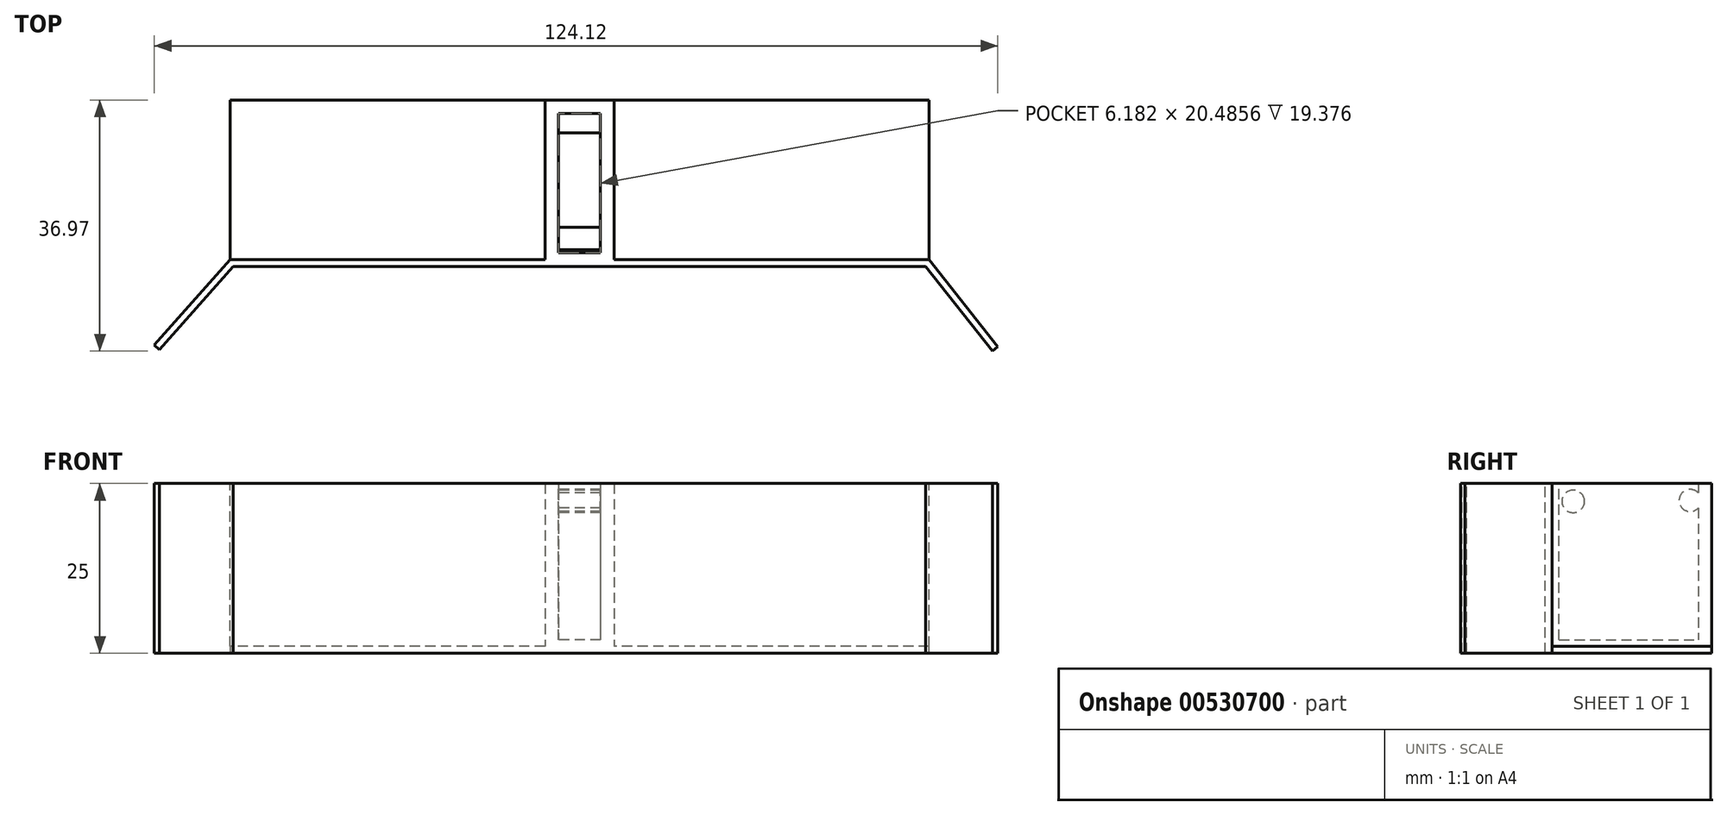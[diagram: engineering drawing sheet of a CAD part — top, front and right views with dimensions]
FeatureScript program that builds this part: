
annotation { "Feature Type Name" : "Feature", "Feature Type Description" : "" }
export const myFeature = defineFeature(function(context is Context, id is Id, definition is map)
    precondition{}
    {
        {
            var Q0;
            Q0=qCreatedBy(makeId("Top.planeOp"),FACE);
            var sketch = newSketch(context, id + "F0", { "sketchPlane" : qUnion([Q0])});
            skLineSegment(sketch, "E0.bottom", {"start": v(51.45, 11.74) * mm, "end": v(-51.45, 11.74) * mm});
            skLineSegment(sketch, "E0.top", {"start": v(51.45, -11.74) * mm, "end": v(-51.45, -11.74) * mm});
            skLineSegment(sketch, "E0.left", {"start": v(51.45, 11.74) * mm, "end": v(51.45, -11.74) * mm});
            skLineSegment(sketch, "E0.right", {"start": v(-51.45, 11.74) * mm, "end": v(-51.45, -11.74) * mm});
            skPoint(sketch, "E0.middle", {"position": v(0, 0) * mm});
            skLineSegment(sketch, "E1", {"start": v(-51.45, -11.74) * mm, "end": v(-62.57, -24.35) * mm});
            skLineSegment(sketch, "E2", {"start": v(51.45, -11.74) * mm, "end": v(61.55, -24.61) * mm});
            skSolve(sketch);
        }
        {
            var Q0;
            Q0=sQuery(id+"F0.wireOp",EDGE,"E2");
            extrude(context, id + "F1", {"bodyType" : ToolBodyType.SURFACE, "surfaceEntities" : qUnion([Q0]), "depth" : 25 * mm, "offsetDistance" : 25 * mm});
        }
        {
            var Q0;
            Q0=sQuery(id+"F0.wireOp",EDGE,"E1");
            extrude(context, id + "F2", {"bodyType" : ToolBodyType.SURFACE, "surfaceEntities" : qUnion([Q0]), "depth" : 25 * mm, "offsetDistance" : 25 * mm});
        }
        {
            var Q0;
            Q0=sQuery(id+"F0.wireOp",EDGE,"E0.top");
            extrude(context, id + "F3", {"bodyType" : ToolBodyType.SURFACE, "surfaceEntities" : qUnion([Q0]), "depth" : 25 * mm, "offsetDistance" : 25 * mm});
        }
        {
            var Q0;
            Q0=makeQuery(id+"F0.imprint","IMPRINT",FACE,{"disambiguationData":[TD([[makeQuery(id+"F0.imprint","IMPRINT",EDGE,{"derivedFrom":sQuery(id+"F0.wireOp",EDGE,"E0.bottom")}),1.0]])]});
            extrude(context, id + "F4", {"entities" : qUnion([Q0]), "depth" : 1 * mm, "offsetDistance" : 25 * mm});
        }
        {
            var Q0;
            Q0=makeQuery(id+"F3.opExtrude","SWEPT_FACE",FACE,{"disambiguationData":[OSD([sQuery(id+"F0.wireOp",EDGE,"E0.top")])]});
            extrude(context, id + "F5", {"entities" : qUnion([Q0]), "operationType" : NewBodyOperationType.ADD, "oppositeDirection" : true, "depth" : 1 * mm, "offsetDistance" : 25 * mm});
        }
        {
            var Q0;
            Q0=makeQuery(id+"F2.opExtrude","SWEPT_FACE",FACE,{"disambiguationData":[OSD([sQuery(id+"F0.wireOp",EDGE,"E1")])]});
            extrude(context, id + "F6", {"entities" : qUnion([Q0]), "operationType" : NewBodyOperationType.ADD, "oppositeDirection" : true, "depth" : 1 * mm, "offsetDistance" : 25 * mm});
        }
        {
            var Q0;
            Q0=makeQuery(id+"F1.opExtrude","SWEPT_FACE",FACE,{"disambiguationData":[OSD([sQuery(id+"F0.wireOp",EDGE,"E2")])]});
            extrude(context, id + "F7", {"entities" : qUnion([Q0]), "operationType" : NewBodyOperationType.ADD, "depth" : 1 * mm, "offsetDistance" : 25 * mm});
        }
        {
            var Q0;
            Q0=makeQuery(id+"F4.opExtrude","CAP_FACE",FACE,{"disambiguationData":[OSD([sQuery(id+"F0.wireOp",EDGE,"E0.bottom"),sQuery(id+"F0.wireOp",EDGE,"E0.top"),sQuery(id+"F0.wireOp",EDGE,"E0.left"),sQuery(id+"F0.wireOp",EDGE,"E0.right")])],"isStart":false});
            var sketch = newSketch(context, id + "F8", { "sketchPlane" : qUnion([Q0])});
            skLineSegment(sketch, "E3.bottom", {"start": v(5.1, -11.74) * mm, "end": v(-5.1, -11.74) * mm});
            skLineSegment(sketch, "E3.top", {"start": v(5.1, 11.74) * mm, "end": v(-5.1, 11.74) * mm});
            skLineSegment(sketch, "E3.left", {"start": v(5.1, -11.74) * mm, "end": v(5.1, 11.74) * mm});
            skLineSegment(sketch, "E3.right", {"start": v(-5.1, -11.74) * mm, "end": v(-5.1, 11.74) * mm});
            skPoint(sketch, "E3.middle", {"position": v(0, 0) * mm});
            skSolve(sketch);
        }
        {
            var Q0;
            Q0=makeQuery(id+"F8.imprint","IMPRINT",FACE,{"disambiguationData":[TD([[makeQuery(id+"F8.imprint","IMPRINT",EDGE,{"derivedFrom":sQuery(id+"F8.wireOp",EDGE,"E3.bottom")}),-1.0]])]});
            extrude(context, id + "F9", {"entities" : qUnion([Q0]), "operationType" : NewBodyOperationType.ADD, "depth" : 24 * mm, "offsetDistance" : 25 * mm});
        }
        {
            var Q0;
            {var subQ0=sQuery(id+"F0.wireOp",EDGE,"E2");var subQ1=sQuery(id+"F0.wireOp",EDGE,"E1");var subQ2=sQuery(id+"F0.wireOp",EDGE,"E0.top");Q0=makeQuery(id+"F9.boolean.opBoolean","MERGE",FACE,{"derivedFrom":[makeQuery(id+"F7.boolean.opBoolean","MERGE",FACE,{"derivedFrom":[makeQuery(id+"F6.boolean.opBoolean","MERGE",FACE,{"derivedFrom":[makeQuery(id+"F5.opExtrude","SWEPT_FACE",FACE,{"disambiguationData":[OSD([subQ2]),TDD([makeQuery(id+"F3.opExtrude","CAP_EDGE",EDGE,{"disambiguationData":[OSD([subQ2])],"isStart":false})])]}),makeQuery(id+"F6.opExtrude","SWEPT_FACE",FACE,{"disambiguationData":[OSD([subQ1]),TDD([makeQuery(id+"F2.opExtrude","CAP_EDGE",EDGE,{"disambiguationData":[OSD([subQ1])],"isStart":false})])]})]}),makeQuery(id+"F7.opExtrude","SWEPT_FACE",FACE,{"disambiguationData":[OSD([subQ0]),TDD([makeQuery(id+"F1.opExtrude","CAP_EDGE",EDGE,{"disambiguationData":[OSD([subQ0])],"isStart":false})])]})]}),makeQuery(id+"F9.opExtrude","CAP_FACE",FACE,{"disambiguationData":[OSD([sQuery(id+"F8.wireOp",EDGE,"E3.bottom"),sQuery(id+"F8.wireOp",EDGE,"E3.top"),sQuery(id+"F8.wireOp",EDGE,"E3.left"),sQuery(id+"F8.wireOp",EDGE,"E3.right")])],"isStart":false})]});}
            shell(context, id + "F10", {"entities" : qUnion([Q0]), "thickness" : 2 * mm});
        }
        {
            var Q0;
            Q0=makeQuery(id+"F9.opExtrude","SWEPT_FACE",FACE,{"disambiguationData":[OSD([sQuery(id+"F8.wireOp",EDGE,"E3.right")])]});
            var sketch = newSketch(context, id + "F11", { "sketchPlane" : qUnion([Q0])});
            skCircle(sketch, "E4", {"center": v(-8.57, 22.5) * mm, "radius": 1.63 * mm});
            skCircle(sketch, "E5", {"center": v(-8.57, 22.5) * mm, "radius": 1.62 * mm});
            skCircle(sketch, "E6", {"center": v(8.66, 22.37) * mm, "radius": 1.66 * mm});
            skSolve(sketch);
        }
        {
            var Q0;
            Q0=makeQuery(id+"F11.imprint","IMPRINT",FACE,{"disambiguationData":[TD([[makeQuery(id+"F11.imprint","IMPRINT",EDGE,{"derivedFrom":sQuery(id+"F11.wireOp",EDGE,"E4")}),-1.0]])]});
            var sketch = newSketch(context, id + "F12", { "sketchPlane" : qUnion([Q0])});
            skSolve(sketch);
        }
        {
            var Q0;
            Q0=makeQuery(id+"F11.imprint","IMPRINT",FACE,{"disambiguationData":[TD([[makeQuery(id+"F11.imprint","IMPRINT",EDGE,{"derivedFrom":sQuery(id+"F11.wireOp",EDGE,"E6")}),1.0]])]});
            extrude(context, id + "F13", {"entities" : qUnion([Q0]), "operationType" : NewBodyOperationType.ADD, "oppositeDirection" : true, "depth" : 10 * mm, "offsetDistance" : 25 * mm});
        }
        {
            var Q0;
            Q0=makeQuery(id+"F12.imprint","IMPRINT",FACE,{"disambiguationData":[TD([[makeQuery(id+"F12.imprint","IMPRINT",EDGE,{"derivedFrom":makeQuery(id+"F11.imprint","IMPRINT",EDGE,{"derivedFrom":sQuery(id+"F11.wireOp",EDGE,"E4")})}),1.0]])]});
            extrude(context, id + "F14", {"entities" : qUnion([Q0]), "operationType" : NewBodyOperationType.ADD, "oppositeDirection" : true, "depth" : 10 * mm, "offsetDistance" : 25 * mm});
        }
    });
